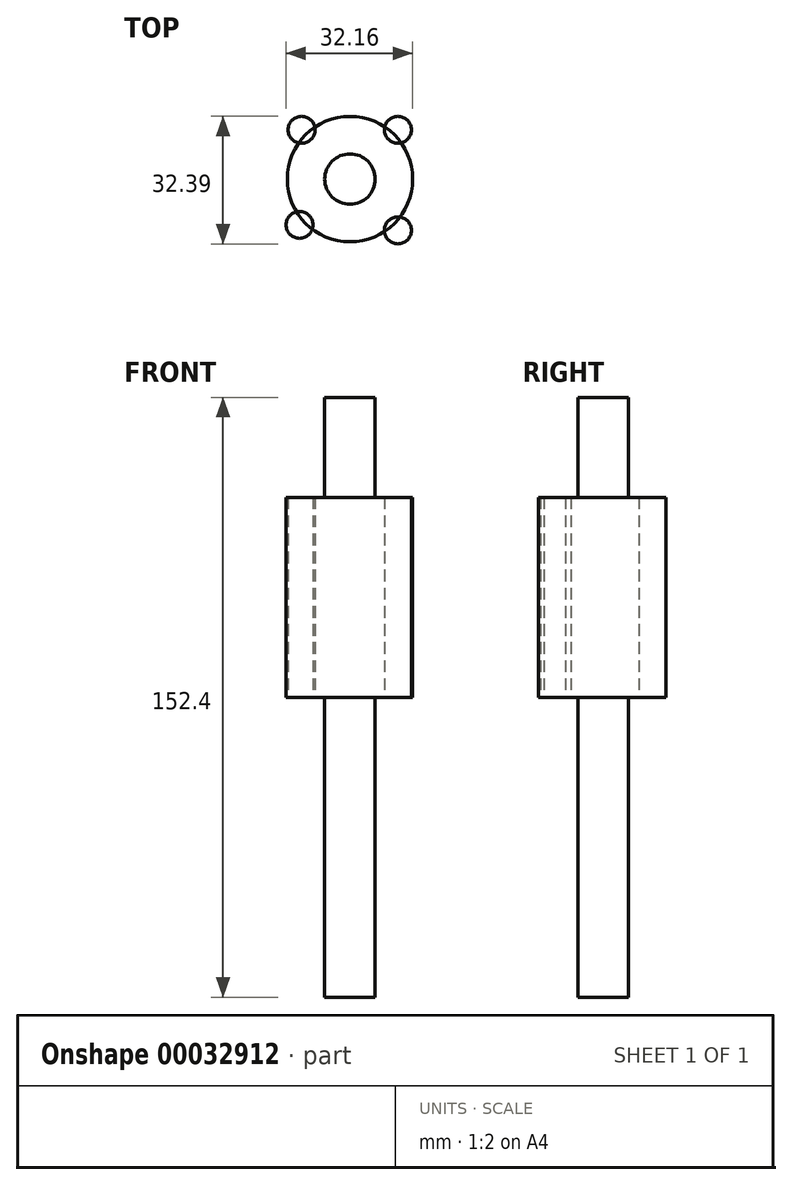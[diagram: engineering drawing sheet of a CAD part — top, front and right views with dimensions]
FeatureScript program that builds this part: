
annotation { "Feature Type Name" : "Feature", "Feature Type Description" : "" }
export const myFeature = defineFeature(function(context is Context, id is Id, definition is map)
    precondition{}
    {
        {
            var Q0;
            Q0=qCreatedBy(makeId("Top.planeOp"),FACE);
            var sketch = newSketch(context, id + "F0", { "sketchPlane" : qUnion([Q0])});
            skCircle(sketch, "E0", {"center": v(0, 0) * mm, "radius": 6.35 * mm});
            skCircle(sketch, "E1", {"center": v(0, 0) * mm, "radius": 15.93 * mm});
            skSolve(sketch);
        }
        {
            var Q0;
            Q0=makeQuery(id+"F0.imprint","IMPRINT",FACE,{"disambiguationData":[TD([[makeQuery(id+"F0.imprint","IMPRINT",EDGE,{"derivedFrom":sQuery(id+"F0.wireOp",EDGE,"E0")}),-1.0]])]});
            extrude(context, id + "F1", {"entities" : qUnion([Q0]), "depth" : 50.8 * mm});
        }
        {
            var Q0;
            Q0=qCreatedBy(makeId("Top.planeOp"),FACE);
            var sketch = newSketch(context, id + "F2", { "sketchPlane" : qUnion([Q0])});
            skCircle(sketch, "E2", {"center": v(-12.28, 12.52) * mm, "radius": 3.43 * mm});
            skSolve(sketch);
        }
        {
            var Q0;
            Q0=makeQuery(id+"F2.imprint","IMPRINT",FACE,{"disambiguationData":[TD([[makeQuery(id+"F2.imprint","IMPRINT",EDGE,{"derivedFrom":sQuery(id+"F2.wireOp",EDGE,"E2")}),1.0]])]});
            extrude(context, id + "F3", {"entities" : qUnion([Q0]), "depth" : 50.8 * mm});
        }
        {
            var Q0;
            Q0=makeQuery(id+"F3.opExtrude","SWEPT_BODY",BODY,{"disambiguationData":[OSD([sQuery(id+"F2.wireOp",EDGE,"E2")])]});
            transform(context, id + "F4", {"entities" : qUnion([Q0]), "transformType" : TransformType.TRANSLATION_3D, "dx" : 24.45 * mm, "dy" : 0 * mm, "dz" : 0 * mm, "makeCopy" : true});
        }
        {
            var Q0;
            Q0=makeQuery(id+"F4.opPattern","COPY",BODY,{"derivedFrom":makeQuery(id+"F3.opExtrude","SWEPT_BODY",BODY,{"disambiguationData":[OSD([sQuery(id+"F2.wireOp",EDGE,"E2")])]}),"instanceName":"1"});
            transform(context, id + "F5", {"entities" : qUnion([Q0]), "transformType" : TransformType.TRANSLATION_3D, "dx" : 0 * mm, "dy" : -25.54 * mm, "dz" : 0 * mm, "makeCopy" : true});
        }
        {
            var Q0;
            Q0=makeQuery(id+"F5.opPattern","COPY",BODY,{"derivedFrom":makeQuery(id+"F4.opPattern","COPY",BODY,{"derivedFrom":makeQuery(id+"F3.opExtrude","SWEPT_BODY",BODY,{"disambiguationData":[OSD([sQuery(id+"F2.wireOp",EDGE,"E2")])]}),"instanceName":"1"}),"instanceName":"1"});
            transform(context, id + "F6", {"entities" : qUnion([Q0]), "transformType" : TransformType.TRANSLATION_3D, "dx" : -24.98 * mm, "dy" : 1.38 * mm, "dz" : 0 * mm, "makeCopy" : true});
        }
        {
            var Q0;
            Q0=qCreatedBy(makeId("Top.planeOp"),FACE);
            var sketch = newSketch(context, id + "F7", { "sketchPlane" : qUnion([Q0])});
            skCircle(sketch, "E3", {"center": v(0, 0) * mm, "radius": 6.4 * mm});
            skSolve(sketch);
        }
        {
            var Q0;
            Q0 = qSketchRegion(id + "F7", true);
            extrude(context, id + "F8", {"entities" : qUnion([Q0]), "operationType" : NewBodyOperationType.ADD, "endBound" : BoundingType.SYMMETRIC, "depth" : 152.4 * mm});
        }
    });
